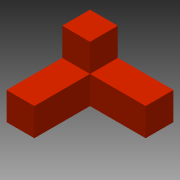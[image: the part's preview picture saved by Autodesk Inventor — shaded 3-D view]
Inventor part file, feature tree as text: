
AUTODESK INVENTOR PART (.ipt)
format: ipt  version: 2015 (Build 190159000, 159)  size: 92,672 bytes
history: native  units: in
note: dims shown in document units (in); Inventor stores cm internally (conversion verified against a paired STEP export)
features: extrude x2, sketch x2
ambient origin geometry x8: Origin, YZ Plane, XZ Plane, XY Plane, X Axis, Y Axis, Z Axis, Center Point
bodies: Solid1 (feature_tree)
feature tree (4):
  extrude  "Extrusion1"  Depth=0.75in
  extrude  "Extrusion2"  Depth=1.5in
  sketch  "Sketch1"  dims[d0=1.5in d1=0.75in]
  sketch  "Sketch2"  dims[d2=0.75in d3=1.5in d4=0.75in d5=0.0in d6=0.75in d7=1.5in d8=0.0in]
